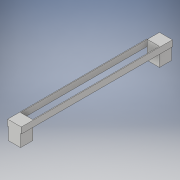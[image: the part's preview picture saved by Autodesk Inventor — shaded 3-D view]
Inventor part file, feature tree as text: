
AUTODESK INVENTOR PART (.ipt)
format: ipt  version: 2018 (Build 220112000, 112)  size: 121,344 bytes
history: native  units: in
note: dims shown in document units (in); Inventor stores cm internally (conversion verified against a paired STEP export)
features: extrude x3, sketch x3
ambient origin geometry x8: Origin, YZ Plane, XZ Plane, XY Plane, X Axis, Y Axis, Z Axis, Center Point
bodies: Solid1 (feature_tree)
feature tree (6):
  extrude  "Extrusion1"  Depth=3.0in TaperAngle=0.0deg
  extrude  "Extrusion2"  Depth=0.125in TaperAngle=0.0deg
  extrude  "Extrusion3"  Depth=20.875in
  sketch  "Sketch1"  dims[d0=2.0in d2=3.0in d3=0.0in]
  sketch  "Sketch2"  dims[d4=1.0in d5=0.125in d6=0.0in]
  sketch  "Sketch3"  dims[d8=0.125in d9=0.0in d10=20.875in]
